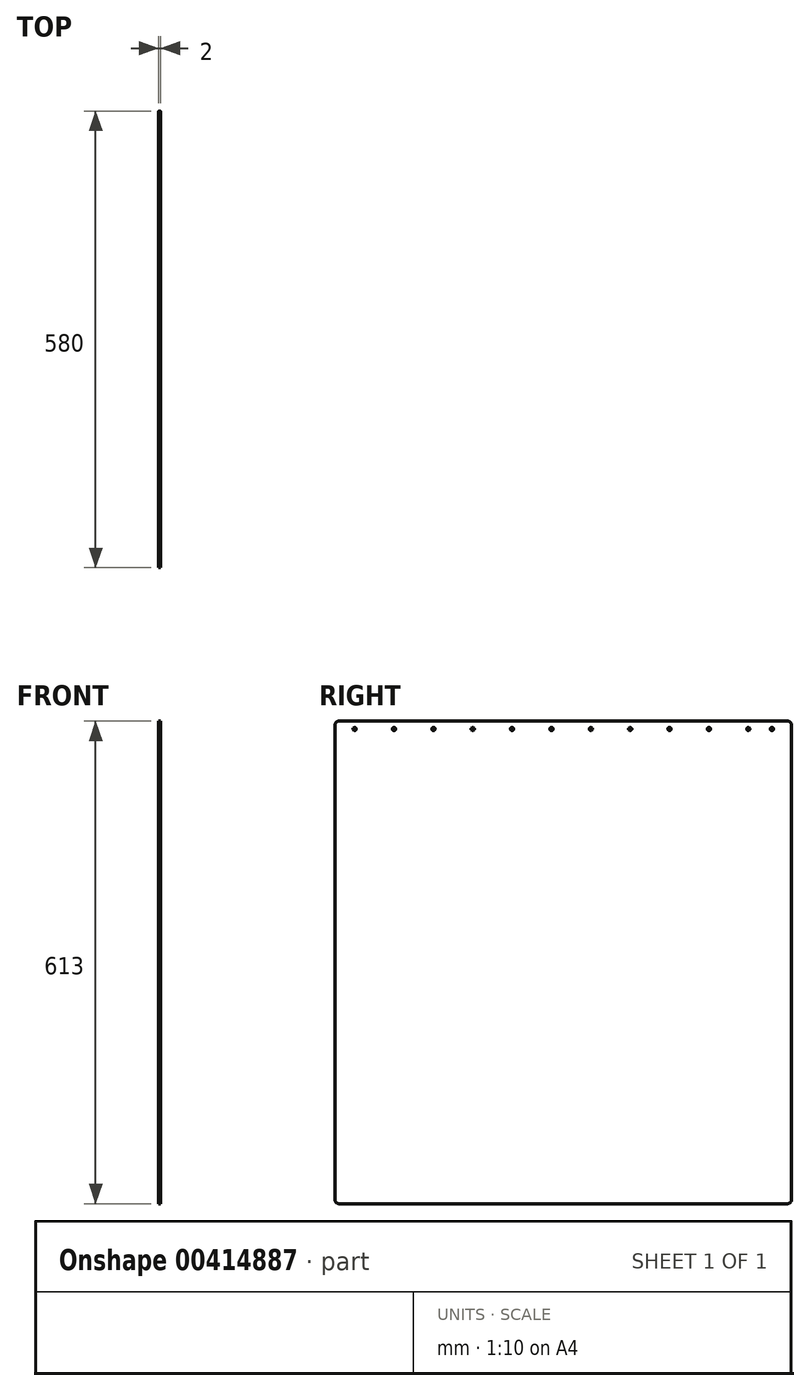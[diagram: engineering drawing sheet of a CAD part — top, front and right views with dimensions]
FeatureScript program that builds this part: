
annotation { "Feature Type Name" : "Feature", "Feature Type Description" : "" }
export const myFeature = defineFeature(function(context is Context, id is Id, definition is map)
    precondition{}
    {
        {
            var Q0;
            Q0=qCreatedBy(makeId("Right.planeOp"),FACE);
            var sketch = newSketch(context, id + "F0", { "sketchPlane" : qUnion([Q0])});
            skLineSegment(sketch, "E0.bottom", {"start": v(0, 0) * mm, "end": v(580, 0) * mm});
            skLineSegment(sketch, "E0.top", {"start": v(0, 613) * mm, "end": v(580, 613) * mm});
            skLineSegment(sketch, "E0.left", {"start": v(0, 0) * mm, "end": v(0, 613) * mm});
            skLineSegment(sketch, "E0.right", {"start": v(580, 0) * mm, "end": v(580, 613) * mm});
            skSolve(sketch);
        }
        {
            var Q0;
            Q0=makeQuery(id+"F0.imprint","IMPRINT",FACE,{"disambiguationData":[TD([[makeQuery(id+"F0.imprint","IMPRINT",EDGE,{"derivedFrom":sQuery(id+"F0.wireOp",EDGE,"E0.bottom")}),1.0]])]});
            extrude(context, id + "F1", {"entities" : qUnion([Q0]), "depth" : 2 * mm});
        }
        {
            var Q0;
            Q0=makeQuery(id+"F1.opExtrude","CAP_FACE",FACE,{"disambiguationData":[OSD([sQuery(id+"F0.wireOp",EDGE,"E0.bottom"),sQuery(id+"F0.wireOp",EDGE,"E0.top"),sQuery(id+"F0.wireOp",EDGE,"E0.left"),sQuery(id+"F0.wireOp",EDGE,"E0.right")])],"isStart":false});
            var sketch = newSketch(context, id + "F2", { "sketchPlane" : qUnion([Q0])});
            skLineSegment(sketch, "E1", {"start": v(25, 603) * mm, "end": v(555, 603) * mm, "construction": true});
            skPoint(sketch, "E2", {"position": v(75, 603) * mm});
            skPoint(sketch, "E3", {"position": v(125, 603) * mm});
            skPoint(sketch, "E4", {"position": v(175, 603) * mm});
            skPoint(sketch, "E5", {"position": v(225, 603) * mm});
            skPoint(sketch, "E6", {"position": v(275, 603) * mm});
            skPoint(sketch, "E7", {"position": v(325, 603) * mm});
            skPoint(sketch, "E8", {"position": v(375, 603) * mm});
            skPoint(sketch, "E9", {"position": v(425, 603) * mm});
            skPoint(sketch, "E10", {"position": v(475, 603) * mm});
            skPoint(sketch, "E11", {"position": v(525, 603) * mm});
            skSolve(sketch);
        }
        {
            var Q0;
            Q0=sQuery(id+"F2.wireOp",VERTEX,"E1.start");
            var Q1;
            Q1=sQuery(id+"F2.wireOp",VERTEX,"E2");
            var Q2;
            Q2=sQuery(id+"F2.wireOp",VERTEX,"E3");
            var Q3;
            Q3=sQuery(id+"F2.wireOp",VERTEX,"E4");
            var Q4;
            Q4=sQuery(id+"F2.wireOp",VERTEX,"E5");
            var Q5;
            Q5=sQuery(id+"F2.wireOp",VERTEX,"E7");
            var Q6;
            Q6=sQuery(id+"F2.wireOp",VERTEX,"E6");
            var Q7;
            Q7=sQuery(id+"F2.wireOp",VERTEX,"E8");
            var Q8;
            Q8=sQuery(id+"F2.wireOp",VERTEX,"E9");
            var Q9;
            Q9=sQuery(id+"F2.wireOp",VERTEX,"E10");
            var Q10;
            Q10=sQuery(id+"F2.wireOp",VERTEX,"E11");
            var Q11;
            Q11=sQuery(id+"F2.wireOp",VERTEX,"E1.end");
            var Q12;
            Q12=makeQuery(id+"F1.opExtrude","SWEPT_BODY",BODY,{"disambiguationData":[OSD([sQuery(id+"F0.wireOp",EDGE,"E0.bottom"),sQuery(id+"F0.wireOp",EDGE,"E0.top"),sQuery(id+"F0.wireOp",EDGE,"E0.left"),sQuery(id+"F0.wireOp",EDGE,"E0.right")])]});
            hole(context, id + "F3", {"style" : HoleStyle.SIMPLE, "endStyle" : HoleEndStyle.THROUGH, "holeDiameter" : 4 * mm, "isTappedThrough" : true, "tappedDepth" : 12 * mm, "tapClearance" : 3, "locations" : qUnion([Q0, Q1, Q2, Q3, Q4, Q5, Q6, Q7, Q8, Q9, Q10, Q11]), "scope" : qUnion([Q12])});
        }
        {
            var Q0;
            Q0=makeQuery(id+"F1.opExtrude","SWEPT_EDGE",EDGE,{"disambiguationData":[OSD([sQuery(id+"F0.wireOp",EDGE,"E0.top"),sQuery(id+"F0.wireOp",EDGE,"E0.left")])]});
            var Q1;
            Q1=makeQuery(id+"F1.opExtrude","SWEPT_EDGE",EDGE,{"disambiguationData":[OSD([sQuery(id+"F0.wireOp",EDGE,"E0.top"),sQuery(id+"F0.wireOp",EDGE,"E0.right")])]});
            var Q2;
            Q2=makeQuery(id+"F1.opExtrude","SWEPT_EDGE",EDGE,{"disambiguationData":[OSD([sQuery(id+"F0.wireOp",EDGE,"E0.bottom"),sQuery(id+"F0.wireOp",EDGE,"E0.left")])]});
            var Q3;
            Q3=makeQuery(id+"F1.opExtrude","SWEPT_EDGE",EDGE,{"disambiguationData":[OSD([sQuery(id+"F0.wireOp",EDGE,"E0.bottom"),sQuery(id+"F0.wireOp",EDGE,"E0.right")])]});
            fillet(context, id + "F4", {"entities" : qUnion([Q0, Q1, Q2, Q3]), "radius" : 5 * mm, "tangentPropagation" : true, "allowEdgeOverflow" : false});
        }
    });
